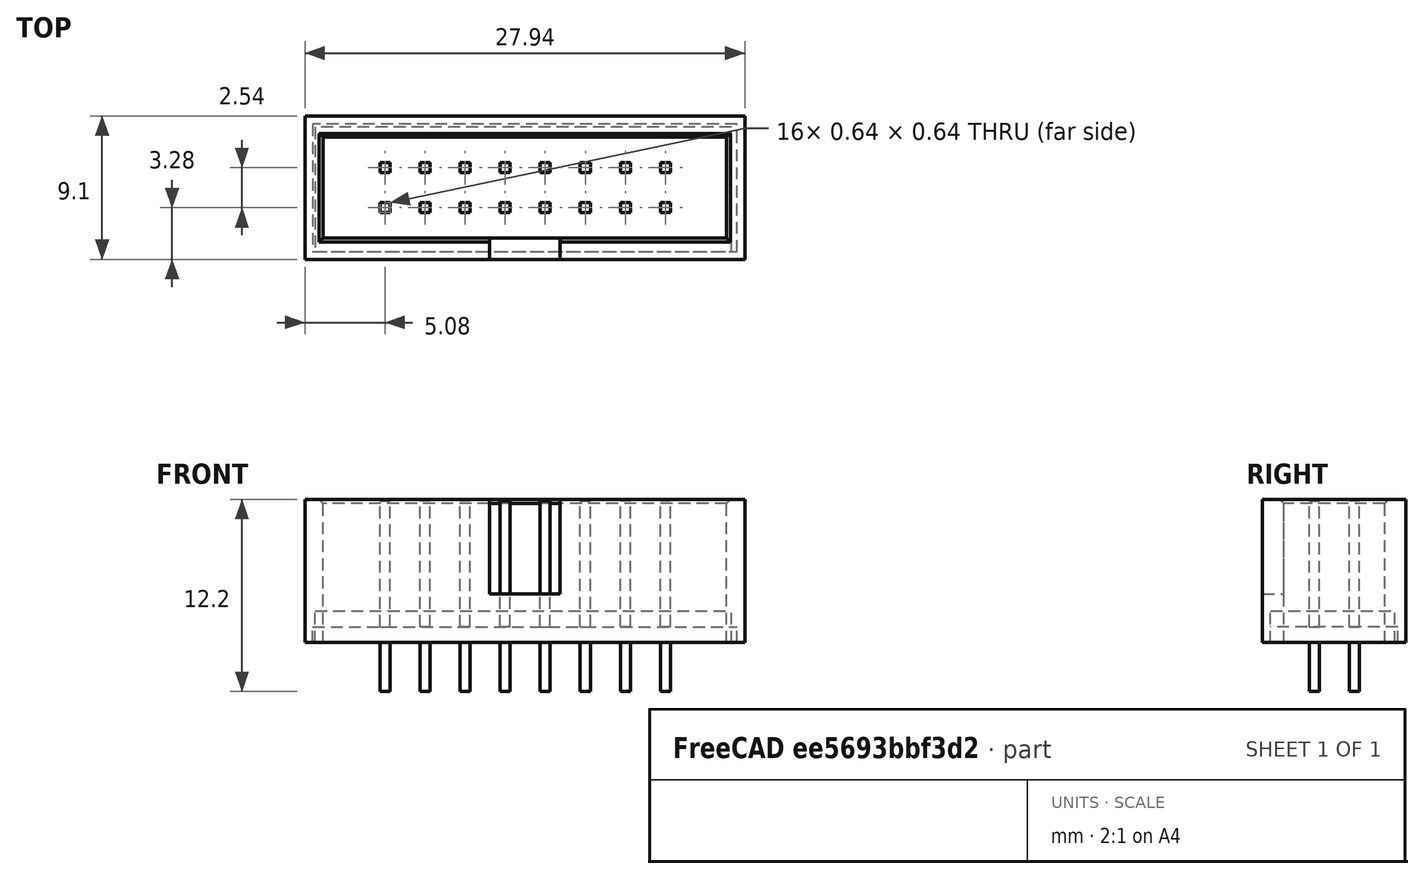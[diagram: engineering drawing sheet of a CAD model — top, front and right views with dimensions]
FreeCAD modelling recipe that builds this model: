
FCSTD DOCUMENT  (FreeCAD 0.17R12831 (Git))
Label: CONN 2x8
License: All rights reserved
LicenseURL: http://en.wikipedia.org/wiki/All_rights_reserved
objects: Part::Feature×2, Sketcher::SketchObject×1, PartDesign::Pad×1, PartDesign::Body×1
note: 6 computed .brp shape members not serialized (recipe doc carries the construction recipe); baked Part::Feature solids carry a one-line shape summary decoded from their .brp

FEATURE [Part::Feature] Part__Feature  label="Body001"
  shape: bbox 26.94 x 8.1 x 12.1 mm, 166 faces (baked)
FEATURE [Part::Feature] Part__Feature001  label="Body"
  shape: bbox 27.94 x 9.1 x 9.1 mm, 18 faces (baked)
FEATURE [Sketcher::SketchObject] Sketch
  MapMode = 5
  Support = -> [XY_Plane]
  sketch-geometry (4):
    g0: LineSegment StartX=0.652279 StartY=0.490472 StartZ=0 EndX=27.09 EndY=0.490472 EndZ=0
    g1: LineSegment StartX=27.09 StartY=0.490472 StartZ=0 EndX=27.09 EndY=8.39627 EndZ=0
    g2: LineSegment StartX=27.09 StartY=8.39627 StartZ=0 EndX=0.652279 EndY=8.39627 EndZ=0
    g3: LineSegment StartX=0.652279 StartY=8.39627 StartZ=0 EndX=0.652279 EndY=0.490472 EndZ=0
  constraints (8):
    c: Coincident(g0,g1)
    c: Coincident(g1,g2)
    c: Coincident(g2,g3)
    c: Coincident(g3,g0)
    c: Horizontal(g0)
    c: Horizontal(g2)
    c: Vertical(g1)
    c: Vertical(g3)
FEATURE [PartDesign::Pad] Pad
  Length = 2
  Length2 = 100
  Profile = -> Sketch
  Type = 0
FEATURE [PartDesign::Body] Body  label="Body002"
  Group = -> [Sketch,Pad]
  Origin = -> Origin
  Tip = -> Pad
